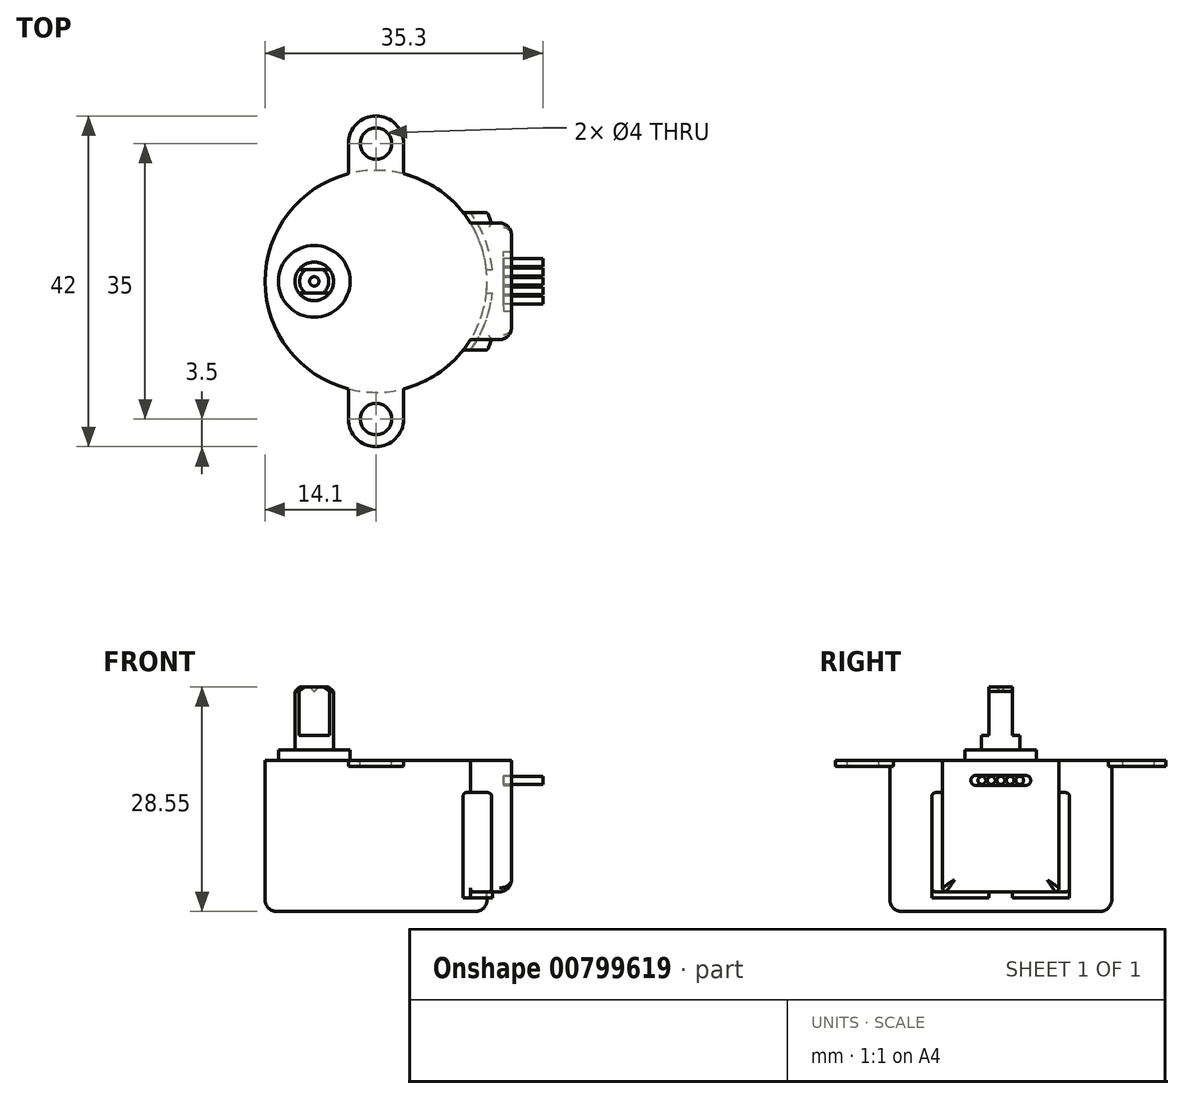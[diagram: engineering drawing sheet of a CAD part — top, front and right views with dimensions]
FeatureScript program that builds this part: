
annotation { "Feature Type Name" : "Feature", "Feature Type Description" : "" }
export const myFeature = defineFeature(function(context is Context, id is Id, definition is map)
    precondition{}
    {
        {
            var Q0;
            Q0=qCreatedBy(makeId("Front.planeOp"),FACE);
            var sketch = newSketch(context, id + "F0", { "sketchPlane" : qUnion([Q0])});
            skLineSegment(sketch, "E0", {"start": v(0, 0) * mm, "end": v(0, 8.75) * mm});
            skLineSegment(sketch, "E1", {"start": v(0.6, 9.35) * mm, "end": v(1.85, 9.35) * mm});
            skLineSegment(sketch, "E2", {"start": v(2.45, 8.75) * mm, "end": v(2.45, 1.35) * mm});
            skLineSegment(sketch, "E3", {"start": v(2.45, 1.35) * mm, "end": v(4.55, 1.35) * mm});
            skLineSegment(sketch, "E4", {"start": v(4.55, 1.35) * mm, "end": v(4.55, 0) * mm});
            skLineSegment(sketch, "E5", {"start": v(4.55, 0) * mm, "end": v(0, 0) * mm});
            skLineSegment(sketch, "E6", {"start": v(1.85, 9.35) * mm, "end": v(2.45, 8.75) * mm});
            skLineSegment(sketch, "E7", {"start": v(0.6, 9.35) * mm, "end": v(0, 8.75) * mm});
            skLineSegment(sketch, "E8", {"start": v(0, 8.75) * mm, "end": v(0, 13.35) * mm, "construction": true});
            skSolve(sketch);
        }
        {
            var Q0;
            Q0=makeQuery(id+"F0.imprint","IMPRINT",FACE,{"disambiguationData":[TD([[makeQuery(id+"F0.imprint","IMPRINT",EDGE,{"derivedFrom":sQuery(id+"F0.wireOp",EDGE,"E0")}),-1.0]])]});
            var Q1;
            Q1=sQuery(id+"F0.wireOp",EDGE,"E8");
            revolve(context, id + "F1", {"entities" : qUnion([Q0]), "axis" : qUnion([Q1]), "revolveType" : RevolveType.FULL});
        }
        {
            var Q0;
            Q0=makeQuery(id+"F1.opRevolve","SWEPT_FACE",FACE,{"disambiguationData":[OSD([sQuery(id+"F0.wireOp",EDGE,"E1")])]});
            var sketch = newSketch(context, id + "F2", { "sketchPlane" : qUnion([Q0])});
            skLineSegment(sketch, "E9", {"start": v(-3.37, 1.5) * mm, "end": v(3.8, 1.5) * mm});
            skLineSegment(sketch, "E10", {"start": v(3.8, 1.5) * mm, "end": v(3.8, 4.5) * mm});
            skLineSegment(sketch, "E11", {"start": v(3.8, 4.5) * mm, "end": v(-3.37, 4.5) * mm});
            skLineSegment(sketch, "E12", {"start": v(-3.37, 4.5) * mm, "end": v(-3.37, 1.5) * mm});
            skLineSegment(sketch, "E13", {"start": v(0, 0) * mm, "end": v(9.16, 0) * mm, "construction": true});
            skLineSegment(sketch, "E14.MirrorCS", {"start": v(-3.37, -4.5) * mm, "end": v(-3.37, -1.5) * mm});
            skLineSegment(sketch, "E15.MirrorCS", {"start": v(3.8, -4.5) * mm, "end": v(-3.37, -4.5) * mm});
            skLineSegment(sketch, "E16.MirrorCS", {"start": v(3.8, -1.5) * mm, "end": v(3.8, -4.5) * mm});
            skLineSegment(sketch, "E17.MirrorCS", {"start": v(-3.37, -1.5) * mm, "end": v(3.8, -1.5) * mm});
            skSolve(sketch);
        }
        {
            var Q0;
            Q0=qSketchRegion(id+"F2",true);
            extrude(context, id + "F3", {"entities" : qUnion([Q0]), "operationType" : NewBodyOperationType.REMOVE, "oppositeDirection" : true, "depth" : 6.2 * mm});
        }
        {
            var Q0;
            Q0=makeQuery(id+"F1.opRevolve","SWEPT_FACE",FACE,{"disambiguationData":[OSD([sQuery(id+"F0.wireOp",EDGE,"E5")])]});
            var sketch = newSketch(context, id + "F4", { "sketchPlane" : qUnion([Q0])});
            skLineSegment(sketch, "E18", {"start": v(0, 0) * mm, "end": v(7.85, 0) * mm, "construction": true});
            skCircle(sketch, "E19", {"center": v(7.85, 0) * mm, "radius": 14.1 * mm});
            skLineSegment(sketch, "E20", {"start": v(0, 0) * mm, "end": v(-4.55, 0) * mm, "construction": true});
            skLineSegment(sketch, "E21", {"start": v(-4.55, 0) * mm, "end": v(-6.25, 0) * mm, "construction": true});
            skSolve(sketch);
        }
        {
            var Q0;
            Q0=qSketchRegion(id+"F4",true);
            extrude(context, id + "F5", {"entities" : qUnion([Q0]), "depth" : 19.2 * mm});
        }
        {
            var Q0;
            Q0=makeQuery(id+"F5.opExtrude","CAP_FACE",FACE,{"disambiguationData":[OSD([sQuery(id+"F0.wireOp",EDGE,"E4"),sQuery(id+"F0.wireOp",EDGE,"E5"),sQuery(id+"F4.wireOp",EDGE,"E19")])],"isStart":true});
            var sketch = newSketch(context, id + "F6", { "sketchPlane" : qUnion([Q0])});
            skLineSegment(sketch, "E22", {"start": v(7.85, 0) * mm, "end": v(7.85, 17.5) * mm, "construction": true});
            skCircle(sketch, "E23", {"center": v(7.85, 17.5) * mm, "radius": 2 * mm});
            skArc(sketch, "E24", {"start": v(11.35, 17.5) * mm, "mid": v(7.85, 21) * mm, "end": v(4.35, 17.5) * mm});
            skLineSegment(sketch, "E25", {"start": v(7.85, 0) * mm, "end": v(11.35, 0) * mm, "construction": true});
            skLineSegment(sketch, "E26", {"start": v(11.35, 0) * mm, "end": v(11.35, 17.5) * mm});
            skLineSegment(sketch, "E27", {"start": v(7.85, 0) * mm, "end": v(4.35, 0) * mm, "construction": true});
            skLineSegment(sketch, "E28", {"start": v(4.35, 0) * mm, "end": v(4.35, 17.5) * mm});
            skLineSegment(sketch, "E29.MirrorCS", {"start": v(4.35, 0) * mm, "end": v(4.35, -17.5) * mm});
            skArc(sketch, "E30.MirrorCS", {"start": v(11.35, -17.5) * mm, "mid": v(7.85, -21) * mm, "end": v(4.35, -17.5) * mm});
            skCircle(sketch, "E31.MirrorC", {"center": v(7.85, -17.5) * mm, "radius": 2 * mm});
            skLineSegment(sketch, "E32.MirrorCS", {"start": v(11.35, 0) * mm, "end": v(11.35, -17.5) * mm});
            skSolve(sketch);
        }
        {
            var Q0;
            Q0=qSketchRegion(id+"F6",true);
            extrude(context, id + "F7", {"entities" : qUnion([Q0]), "oppositeDirection" : true, "depth" : 0.75 * mm});
        }
        {
            var Q0;
            Q0=makeQuery(id+"F7.opExtrude","SWEPT_BODY",BODY,{"disambiguationData":[OSD([sQuery(id+"F6.wireOp",EDGE,"E23"),sQuery(id+"F6.wireOp",EDGE,"E24"),sQuery(id+"F6.wireOp",EDGE,"E26"),sQuery(id+"F6.wireOp",EDGE,"E28"),sQuery(id+"F6.wireOp",EDGE,"E29.MirrorCS"),sQuery(id+"F6.wireOp",EDGE,"E32.MirrorCS"),sQuery(id+"F6.wireOp",EDGE,"E30.MirrorCS"),sQuery(id+"F6.wireOp",EDGE,"E31.MirrorC")])]});
            var Q1;
            Q1=makeQuery(id+"F5.opExtrude","SWEPT_BODY",BODY,{"disambiguationData":[OSD([sQuery(id+"F0.wireOp",EDGE,"E4"),sQuery(id+"F0.wireOp",EDGE,"E5"),sQuery(id+"F4.wireOp",EDGE,"E19")])]});
            booleanBodies(context, id + "F8", {"operationType" : BooleanOperationType.UNION, "tools" : qUnion([Q0, Q1])});
        }
        {
            var Q0;
            Q0=makeQuery(id+"F8.opBoolean","MERGE",FACE,{"derivedFrom":[makeQuery(id+"F5.opExtrude","CAP_FACE",FACE,{"disambiguationData":[OSD([sQuery(id+"F4.wireOp",EDGE,"E19")])],"isStart":true}),makeQuery(id+"F7.opExtrude","CAP_FACE",FACE,{"disambiguationData":[OSD([sQuery(id+"F6.wireOp",EDGE,"E23"),sQuery(id+"F6.wireOp",EDGE,"E24"),sQuery(id+"F6.wireOp",EDGE,"E26"),sQuery(id+"F6.wireOp",EDGE,"E28"),sQuery(id+"F6.wireOp",EDGE,"E29.MirrorCS"),sQuery(id+"F6.wireOp",EDGE,"E32.MirrorCS"),sQuery(id+"F6.wireOp",EDGE,"E30.MirrorCS"),sQuery(id+"F6.wireOp",EDGE,"E31.MirrorC")])],"isStart":true})]});
            var sketch = newSketch(context, id + "F9", { "sketchPlane" : qUnion([Q0])});
            skLineSegment(sketch, "E33", {"start": v(7.85, 0) * mm, "end": v(25.05, 0) * mm, "construction": true});
            skPoint(sketch, "E33.endSnap0", {"position": v(21.95, 0) * mm});
            skLineSegment(sketch, "E34", {"start": v(25.05, 0) * mm, "end": v(25.05, 7.4) * mm});
            skLineSegment(sketch, "E35", {"start": v(25.05, 7.4) * mm, "end": v(7.85, 7.4) * mm});
            skLineSegment(sketch, "E36", {"start": v(7.85, 7.4) * mm, "end": v(7.85, 0) * mm});
            skLineSegment(sketch, "E37.MirrorCS", {"start": v(7.85, -7.4) * mm, "end": v(7.85, 0) * mm});
            skLineSegment(sketch, "E38.MirrorCS", {"start": v(25.05, -7.4) * mm, "end": v(7.85, -7.4) * mm});
            skLineSegment(sketch, "E39.MirrorCS", {"start": v(25.05, 0) * mm, "end": v(25.05, -7.4) * mm});
            skSolve(sketch);
        }
        {
            var Q0;
            {var subQ1=sQuery(id+"F9.wireOp",EDGE,"E34");Q0=makeQuery(id+"F9.imprint","IMPRINT",FACE,{"disambiguationData":[TD([[makeQuery(id+"F9.imprint","IMPRINT",EDGE,{"derivedFrom":subQ1}),1.0]])]});}
            extrude(context, id + "F10", {"entities" : qUnion([Q0]), "operationType" : NewBodyOperationType.ADD, "oppositeDirection" : true, "depth" : 16.7 * mm});
        }
        {
            var Q0;
            Q0=makeQuery(id+"F10.opExtrude","CAP_FACE",FACE,{"disambiguationData":[OSD([sQuery(id+"F4.wireOp",EDGE,"E19"),sQuery(id+"F9.wireOp",EDGE,"E34"),sQuery(id+"F9.wireOp",EDGE,"E35"),sQuery(id+"F9.wireOp",EDGE,"E38.MirrorCS"),sQuery(id+"F9.wireOp",EDGE,"E39.MirrorCS")])],"isStart":false});
            var sketch = newSketch(context, id + "F11", { "sketchPlane" : qUnion([Q0])});
            skLineSegment(sketch, "E40", {"start": v(25.05, 0) * mm, "end": v(21.95, 0) * mm, "construction": true});
            skLineSegment(sketch, "E41", {"start": v(22.55, 0) * mm, "end": v(22.55, 7.4) * mm});
            skLineSegment(sketch, "E42", {"start": v(22.55, 7.4) * mm, "end": v(22.05, 8.75) * mm});
            skLineSegment(sketch, "E43", {"start": v(22.05, 8.75) * mm, "end": v(18.9, 8.75) * mm});
            skLineSegment(sketch, "E44", {"start": v(18.9, 8.75) * mm, "end": v(18.9, 0) * mm});
            skLineSegment(sketch, "E45.MirrorCS", {"start": v(22.55, 0) * mm, "end": v(22.55, -7.4) * mm});
            skLineSegment(sketch, "E46.MirrorCS", {"start": v(22.55, -7.4) * mm, "end": v(22.05, -8.75) * mm});
            skLineSegment(sketch, "E47.MirrorCS", {"start": v(22.05, -8.75) * mm, "end": v(18.9, -8.75) * mm});
            skLineSegment(sketch, "E48.MirrorCS", {"start": v(18.9, -8.75) * mm, "end": v(18.9, 0) * mm});
            skSolve(sketch);
        }
        {
            var Q0;
            {var subQ3=sQuery(id+"F11.wireOp",EDGE,"E42");Q0=makeQuery(id+"F11.imprint","IMPRINT",FACE,{"disambiguationData":[TD([[makeQuery(id+"F11.imprint","IMPRINT",EDGE,{"derivedFrom":subQ3}),1.0]])]});}
            var Q1;
            {var subQ3=sQuery(id+"F11.wireOp",EDGE,"E41");Q1=makeQuery(id+"F11.imprint","IMPRINT",FACE,{"disambiguationData":[TD([[makeQuery(id+"F11.imprint","IMPRINT",EDGE,{"derivedFrom":subQ3}),1.0]])]});}
            extrude(context, id + "F12", {"entities" : qUnion([Q0, Q1]), "operationType" : NewBodyOperationType.ADD, "oppositeDirection" : true, "depth" : 12.6 * mm});
        }
        {
            var Q0;
            Q0=makeQuery(id+"F12.boolean.opBoolean","MERGE",FACE,{"derivedFrom":[makeQuery(id+"F10.opExtrude","CAP_FACE",FACE,{"disambiguationData":[OSD([sQuery(id+"F4.wireOp",EDGE,"E19"),sQuery(id+"F9.wireOp",EDGE,"E34"),sQuery(id+"F9.wireOp",EDGE,"E35"),sQuery(id+"F9.wireOp",EDGE,"E38.MirrorCS"),sQuery(id+"F9.wireOp",EDGE,"E39.MirrorCS")])],"isStart":false}),makeQuery(id+"F12.opExtrude","CAP_FACE",FACE,{"disambiguationData":[OSD([sQuery(id+"F11.wireOp",EDGE,"E41"),sQuery(id+"F11.wireOp",EDGE,"E42"),sQuery(id+"F11.wireOp",EDGE,"E43"),sQuery(id+"F11.wireOp",EDGE,"E44"),sQuery(id+"F11.wireOp",EDGE,"E45.MirrorCS"),sQuery(id+"F11.wireOp",EDGE,"E46.MirrorCS"),sQuery(id+"F11.wireOp",EDGE,"E47.MirrorCS"),sQuery(id+"F11.wireOp",EDGE,"E48.MirrorCS")])],"isStart":true})]});
            var sketch = newSketch(context, id + "F13", { "sketchPlane" : qUnion([Q0])});
            skLineSegment(sketch, "E49", {"start": v(25.05, 0) * mm, "end": v(7.85, 0) * mm, "construction": true});
            skArc(sketch, "E50", {"start": v(18.9, -8.75) * mm, "mid": v(20.9, -5.33) * mm, "end": v(21.87, -1.5) * mm});
            skArc(sketch, "E51", {"start": v(19.84, -8.75) * mm, "mid": v(21.71, -5.3) * mm, "end": v(22.62, -1.5) * mm});
            skLineSegment(sketch, "E52", {"start": v(18.9, -8.75) * mm, "end": v(19.84, -8.75) * mm});
            skLineSegment(sketch, "E53", {"start": v(21.87, -1.5) * mm, "end": v(22.62, -1.5) * mm});
            skLineSegment(sketch, "E54.MirrorCS", {"start": v(21.87, 1.5) * mm, "end": v(22.62, 1.5) * mm});
            skArc(sketch, "E55.MirrorCS", {"start": v(19.84, 8.75) * mm, "mid": v(21.71, 5.3) * mm, "end": v(22.62, 1.5) * mm});
            skArc(sketch, "E56.MirrorCS", {"start": v(18.9, 8.75) * mm, "mid": v(20.9, 5.33) * mm, "end": v(21.87, 1.5) * mm});
            skLineSegment(sketch, "E57.MirrorCS", {"start": v(18.9, 8.75) * mm, "end": v(19.84, 8.75) * mm});
            skSolve(sketch);
        }
        {
            var Q0;
            Q0=makeQuery(id+"F13.imprint","IMPRINT",FACE,{"disambiguationData":[TD([[makeQuery(id+"F13.imprint","IMPRINT",EDGE,{"derivedFrom":sQuery(id+"F13.wireOp",EDGE,"E50")}),-1.0]])]});
            var Q1;
            Q1=makeQuery(id+"F13.imprint","IMPRINT",FACE,{"disambiguationData":[TD([[makeQuery(id+"F13.imprint","IMPRINT",EDGE,{"derivedFrom":sQuery(id+"F13.wireOp",EDGE,"E54.MirrorCS")}),1.0]])]});
            extrude(context, id + "F14", {"entities" : qUnion([Q0, Q1]), "operationType" : NewBodyOperationType.ADD, "depth" : 0.75 * mm});
        }
        {
            var Q0;
            Q0=makeQuery(id+"F10.opExtrude","SWEPT_EDGE",EDGE,{"disambiguationData":[OSD([sQuery(id+"F9.wireOp",EDGE,"E38.MirrorCS"),sQuery(id+"F9.wireOp",EDGE,"E39.MirrorCS")])]});
            var Q1;
            Q1=makeQuery(id+"F10.opExtrude","SWEPT_EDGE",EDGE,{"disambiguationData":[OSD([sQuery(id+"F9.wireOp",EDGE,"E34"),sQuery(id+"F9.wireOp",EDGE,"E35")])]});
            var Q2;
            Q2=makeQuery(id+"F10.opExtrude","CAP_EDGE",EDGE,{"disambiguationData":[OSD([sQuery(id+"F9.wireOp",EDGE,"E34"),sQuery(id+"F9.wireOp",EDGE,"E39.MirrorCS")])],"isStart":false});
            var Q3;
            Q3=makeQuery(id+"F5.opExtrude","CAP_EDGE",EDGE,{"disambiguationData":[OSD([sQuery(id+"F4.wireOp",EDGE,"E19")])],"isStart":false});
            fillet(context, id + "F15", {"entities" : qUnion([Q0, Q1, Q2, Q3]), "radius" : 1.5 * mm, "tangentPropagation" : true, "allowEdgeOverflow" : false});
        }
        {
            var Q0;
            Q0=makeQuery(id+"F10.opExtrude","CAP_EDGE",EDGE,{"disambiguationData":[OSD([sQuery(id+"F9.wireOp",EDGE,"E35")])],"isStart":false});
            var Q1;
            Q1=makeQuery(id+"F12.opExtrude","CAP_EDGE",EDGE,{"disambiguationData":[OSD([sQuery(id+"F11.wireOp",EDGE,"E46.MirrorCS")])],"isStart":true});
            var Q2;
            Q2=makeQuery(id+"F12.opExtrude","CAP_EDGE",EDGE,{"disambiguationData":[OSD([sQuery(id+"F11.wireOp",EDGE,"E47.MirrorCS")])],"isStart":true});
            var Q3;
            Q3=makeQuery(id+"F12.opExtrude","SWEPT_EDGE",EDGE,{"disambiguationData":[OSD([sQuery(id+"F11.wireOp",EDGE,"E46.MirrorCS"),sQuery(id+"F11.wireOp",EDGE,"E47.MirrorCS")])]});
            var Q4;
            Q4=makeQuery(id+"F12.opExtrude","CAP_EDGE",EDGE,{"disambiguationData":[OSD([sQuery(id+"F11.wireOp",EDGE,"E46.MirrorCS")])],"isStart":false});
            var Q5;
            Q5=makeQuery(id+"F12.opExtrude","CAP_EDGE",EDGE,{"disambiguationData":[OSD([sQuery(id+"F11.wireOp",EDGE,"E47.MirrorCS")])],"isStart":false});
            var Q6;
            Q6=makeQuery(id+"F10.opExtrude","CAP_EDGE",EDGE,{"disambiguationData":[OSD([sQuery(id+"F9.wireOp",EDGE,"E38.MirrorCS")])],"isStart":false});
            var Q7;
            Q7=makeQuery(id+"F12.opExtrude","CAP_EDGE",EDGE,{"disambiguationData":[OSD([sQuery(id+"F11.wireOp",EDGE,"E42")])],"isStart":true});
            var Q8;
            Q8=makeQuery(id+"F12.opExtrude","CAP_EDGE",EDGE,{"disambiguationData":[OSD([sQuery(id+"F11.wireOp",EDGE,"E43")])],"isStart":true});
            var Q9;
            Q9=makeQuery(id+"F12.opExtrude","SWEPT_EDGE",EDGE,{"disambiguationData":[OSD([sQuery(id+"F11.wireOp",EDGE,"E42"),sQuery(id+"F11.wireOp",EDGE,"E43")])]});
            var Q10;
            Q10=makeQuery(id+"F12.opExtrude","CAP_EDGE",EDGE,{"disambiguationData":[OSD([sQuery(id+"F11.wireOp",EDGE,"E42")])],"isStart":false});
            var Q11;
            Q11=makeQuery(id+"F12.opExtrude","CAP_EDGE",EDGE,{"disambiguationData":[OSD([sQuery(id+"F11.wireOp",EDGE,"E43")])],"isStart":false});
            fillet(context, id + "F16", {"entities" : qUnion([Q0, Q1, Q2, Q3, Q4, Q5, Q6, Q7, Q8, Q9, Q10, Q11]), "radius" : 0.5 * mm, "tangentPropagation" : true, "allowEdgeOverflow" : false});
        }
        {
            var Q0;
            Q0=makeQuery(id+"F10.opExtrude","SWEPT_FACE",FACE,{"disambiguationData":[OSD([sQuery(id+"F9.wireOp",EDGE,"E34"),sQuery(id+"F9.wireOp",EDGE,"E39.MirrorCS")])]});
            var sketch = newSketch(context, id + "F17", { "sketchPlane" : qUnion([Q0])});
            skLineSegment(sketch, "E58", {"start": v(0, 0) * mm, "end": v(0, -2.55) * mm, "construction": true});
            skLineSegment(sketch, "E59", {"start": v(0, -2.55) * mm, "end": v(-3.15, -2.55) * mm, "construction": true});
            skArc(sketch, "E60", {"start": v(-3.15, -1.9) * mm, "mid": v(-3.8, -2.55) * mm, "end": v(-3.15, -3.2) * mm});
            skLineSegment(sketch, "E61", {"start": v(-3.15, -1.9) * mm, "end": v(0, -1.9) * mm});
            skPoint(sketch, "E61.endSnap0", {"position": v(0, -1.27) * mm});
            skLineSegment(sketch, "E62", {"start": v(-3.15, -3.2) * mm, "end": v(0, -3.2) * mm});
            skLineSegment(sketch, "E63.MirrorCS", {"start": v(3.15, -1.9) * mm, "end": v(0, -1.9) * mm});
            skArc(sketch, "E64.MirrorCS", {"start": v(3.15, -1.9) * mm, "mid": v(3.8, -2.55) * mm, "end": v(3.15, -3.2) * mm});
            skLineSegment(sketch, "E65.MirrorCS", {"start": v(3.15, -3.2) * mm, "end": v(0, -3.2) * mm});
            skSolve(sketch);
        }
        {
            var Q0;
            Q0=makeQuery(id+"F17.imprint","IMPRINT",FACE,{"disambiguationData":[TD([[makeQuery(id+"F17.imprint","IMPRINT",EDGE,{"derivedFrom":sQuery(id+"F17.wireOp",EDGE,"E60")}),1.0]])]});
            extrude(context, id + "F18", {"entities" : qUnion([Q0]), "operationType" : NewBodyOperationType.REMOVE, "oppositeDirection" : true, "depth" : 1 * mm});
        }
        {
            var Q0;
            Q0=makeQuery(id+"F18.boolean.opBoolean","COPY",FACE,{"derivedFrom":makeQuery(id+"F18.opExtrude","CAP_FACE",FACE,{"disambiguationData":[OSD([sQuery(id+"F17.wireOp",EDGE,"E60"),sQuery(id+"F17.wireOp",EDGE,"E61"),sQuery(id+"F17.wireOp",EDGE,"E62"),sQuery(id+"F17.wireOp",EDGE,"E63.MirrorCS"),sQuery(id+"F17.wireOp",EDGE,"E64.MirrorCS"),sQuery(id+"F17.wireOp",EDGE,"E65.MirrorCS")])],"isStart":false})});
            var sketch = newSketch(context, id + "F19", { "sketchPlane" : qUnion([Q0])});
            skLineSegment(sketch, "E66", {"start": v(0, -3.2) * mm, "end": v(0, -1.9) * mm, "construction": true});
            skLineSegment(sketch, "E67", {"start": v(0, -2.55) * mm, "end": v(1.2, -2.55) * mm, "construction": true});
            skLineSegment(sketch, "E68", {"start": v(1.2, -2.55) * mm, "end": v(2.4, -2.55) * mm, "construction": true});
            skLineSegment(sketch, "E69", {"start": v(0, -2.55) * mm, "end": v(-1.2, -2.55) * mm, "construction": true});
            skLineSegment(sketch, "E70", {"start": v(-1.2, -2.55) * mm, "end": v(-2.4, -2.55) * mm, "construction": true});
            skCircle(sketch, "E71", {"center": v(0, -2.55) * mm, "radius": 0.5 * mm});
            skCircle(sketch, "E72", {"center": v(-1.2, -2.55) * mm, "radius": 0.5 * mm});
            skCircle(sketch, "E73", {"center": v(-2.4, -2.55) * mm, "radius": 0.5 * mm});
            skCircle(sketch, "E74", {"center": v(1.2, -2.55) * mm, "radius": 0.5 * mm});
            skCircle(sketch, "E75", {"center": v(2.4, -2.55) * mm, "radius": 0.5 * mm});
            skSolve(sketch);
        }
        {
            var Q0;
            Q0=makeQuery(id+"F19.imprint","IMPRINT",FACE,{"disambiguationData":[TD([[makeQuery(id+"F19.imprint","IMPRINT",EDGE,{"derivedFrom":sQuery(id+"F19.wireOp",EDGE,"E73")}),1.0]])]});
            extrude(context, id + "F20", {"entities" : qUnion([Q0]), "depth" : 5 * mm});
        }
        {
            var Q0;
            Q0=makeQuery(id+"F19.imprint","IMPRINT",FACE,{"disambiguationData":[TD([[makeQuery(id+"F19.imprint","IMPRINT",EDGE,{"derivedFrom":sQuery(id+"F19.wireOp",EDGE,"E72")}),1.0]])]});
            extrude(context, id + "F21", {"entities" : qUnion([Q0]), "depth" : 5 * mm});
        }
        {
            var Q0;
            Q0=makeQuery(id+"F19.imprint","IMPRINT",FACE,{"disambiguationData":[TD([[makeQuery(id+"F19.imprint","IMPRINT",EDGE,{"derivedFrom":sQuery(id+"F19.wireOp",EDGE,"E71")}),1.0]])]});
            extrude(context, id + "F22", {"entities" : qUnion([Q0]), "depth" : 5 * mm});
        }
        {
            var Q0;
            Q0=makeQuery(id+"F19.imprint","IMPRINT",FACE,{"disambiguationData":[TD([[makeQuery(id+"F19.imprint","IMPRINT",EDGE,{"derivedFrom":sQuery(id+"F19.wireOp",EDGE,"E74")}),1.0]])]});
            extrude(context, id + "F23", {"entities" : qUnion([Q0]), "depth" : 5 * mm});
        }
        {
            var Q0;
            Q0=makeQuery(id+"F19.imprint","IMPRINT",FACE,{"disambiguationData":[TD([[makeQuery(id+"F19.imprint","IMPRINT",EDGE,{"derivedFrom":sQuery(id+"F19.wireOp",EDGE,"E75")}),1.0]])]});
            extrude(context, id + "F24", {"entities" : qUnion([Q0]), "depth" : 5 * mm});
        }
        {
            var Q0;
            Q0=makeQuery(id+"F18.boolean.opBoolean","COPY",FACE,{"derivedFrom":makeQuery(id+"F18.opExtrude","CAP_FACE",FACE,{"disambiguationData":[OSD([sQuery(id+"F17.wireOp",EDGE,"E60"),sQuery(id+"F17.wireOp",EDGE,"E61"),sQuery(id+"F17.wireOp",EDGE,"E62"),sQuery(id+"F17.wireOp",EDGE,"E63.MirrorCS"),sQuery(id+"F17.wireOp",EDGE,"E64.MirrorCS"),sQuery(id+"F17.wireOp",EDGE,"E65.MirrorCS")])],"isStart":false})});
            var sketch = newSketch(context, id + "F25", { "sketchPlane" : qUnion([Q0])});
            skCircle(sketch, "E76.0", {"center": v(-2.4, -2.55) * mm, "radius": 0.5 * mm});
            skCircle(sketch, "E77.0", {"center": v(-1.2, -2.55) * mm, "radius": 0.5 * mm});
            skCircle(sketch, "E78.0", {"center": v(0, -2.55) * mm, "radius": 0.5 * mm});
            skCircle(sketch, "E79.0", {"center": v(1.2, -2.55) * mm, "radius": 0.5 * mm});
            skCircle(sketch, "E80.0", {"center": v(2.4, -2.55) * mm, "radius": 0.5 * mm});
            skSolve(sketch);
        }
    });
